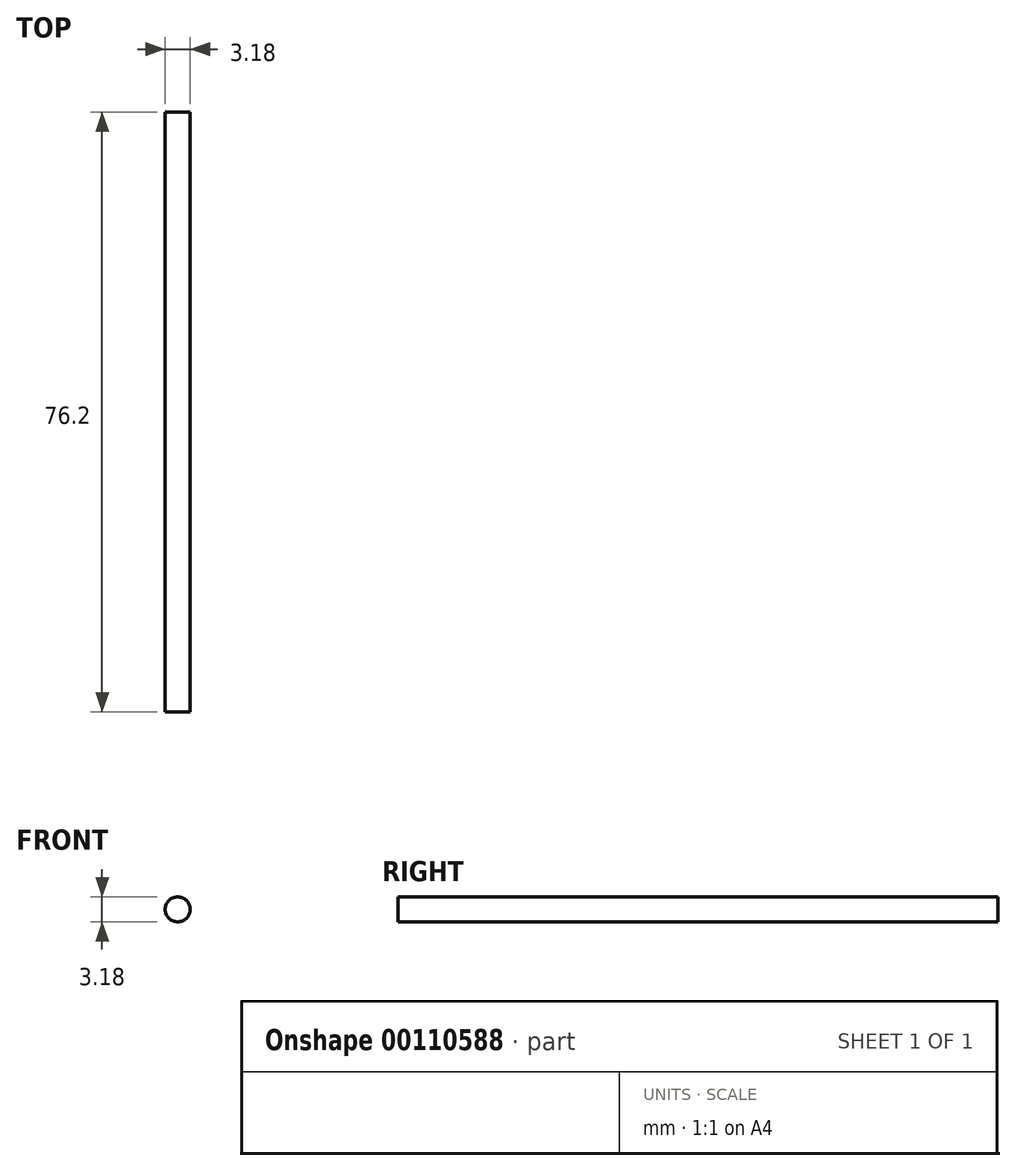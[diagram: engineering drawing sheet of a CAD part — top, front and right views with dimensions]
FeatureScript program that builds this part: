
annotation { "Feature Type Name" : "Feature", "Feature Type Description" : "" }
export const myFeature = defineFeature(function(context is Context, id is Id, definition is map)
    precondition{}
    {
        {
            var Q0;
            Q0=qCreatedBy(makeId("Front.planeOp"),FACE);
            var sketch = newSketch(context, id + "F0", { "sketchPlane" : qUnion([Q0])});
            skCircle(sketch, "E0", {"center": v(0, 0) * mm, "radius": 1.59 * mm});
            skSolve(sketch);
        }
        {
            var Q0;
            Q0=qSketchRegion(id+"F0",true);
            extrude(context, id + "F1", {"entities" : qUnion([Q0]), "depth" : 76.2 * mm});
        }
    });
